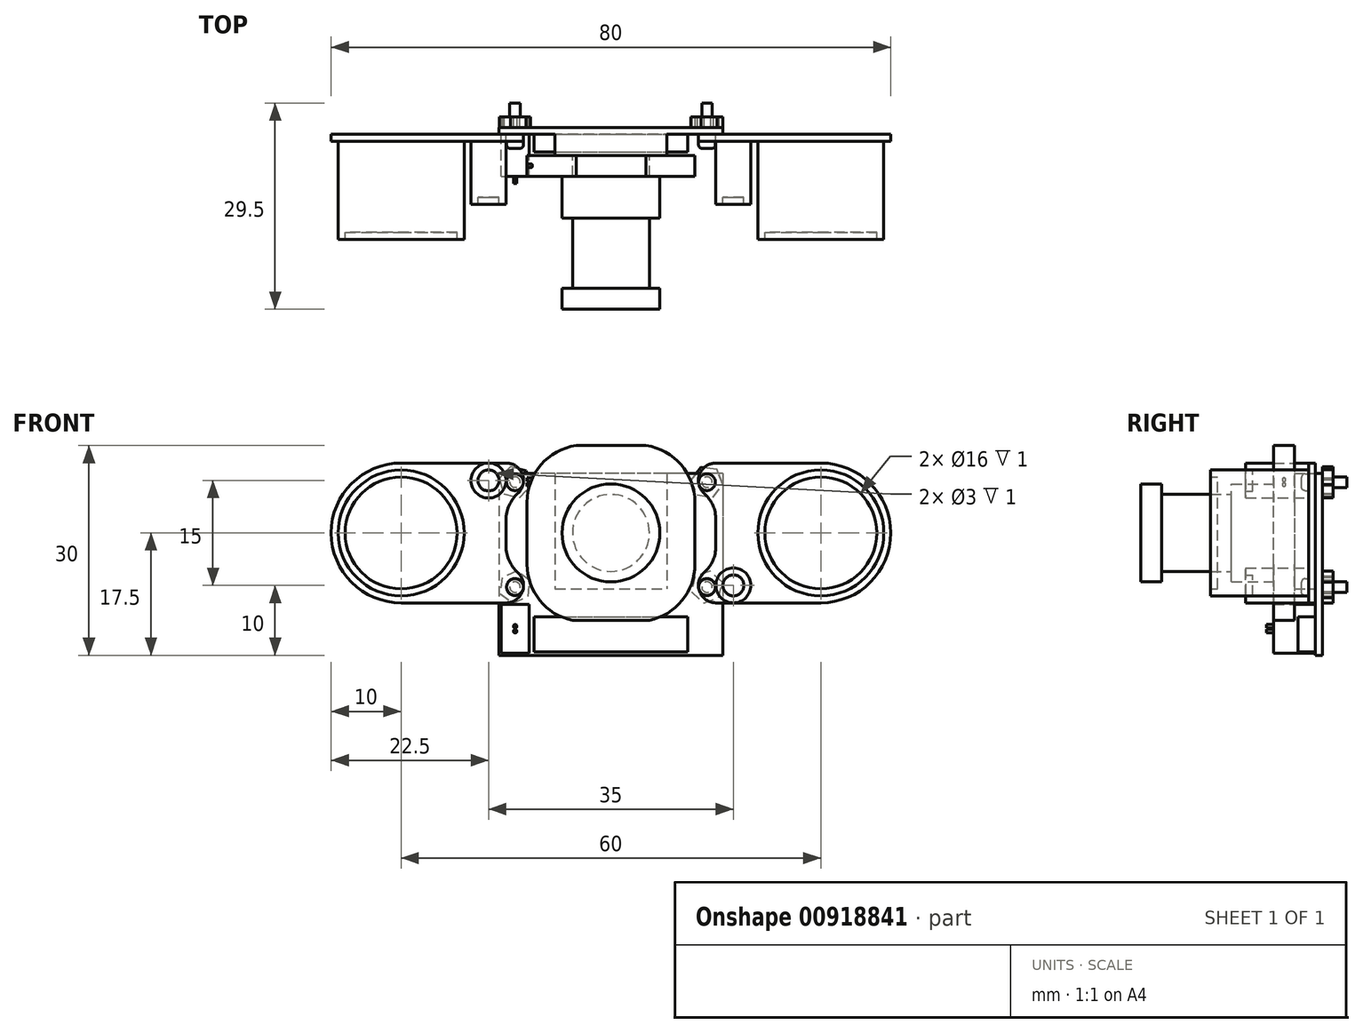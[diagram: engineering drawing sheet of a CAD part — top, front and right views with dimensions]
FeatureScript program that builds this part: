
annotation { "Feature Type Name" : "Feature", "Feature Type Description" : "" }
export const myFeature = defineFeature(function(context is Context, id is Id, definition is map)
    precondition{}
    {
        {
            var Q0;
            Q0=qCreatedBy(makeId("Front.planeOp"),FACE);
            var sketch = newSketch(context, id + "F0", { "sketchPlane" : qUnion([Q0])});
            skLineSegment(sketch, "E0.bottom", {"start": v(16, 13) * mm, "end": v(-16, 13) * mm});
            skLineSegment(sketch, "E0.top", {"start": v(16, -13) * mm, "end": v(-16, -13) * mm});
            skLineSegment(sketch, "E0.left", {"start": v(16, 13) * mm, "end": v(16, -13) * mm});
            skLineSegment(sketch, "E0.right", {"start": v(-16, 13) * mm, "end": v(-16, -13) * mm});
            skPoint(sketch, "E0.middle", {"position": v(0, 0) * mm});
            skSolve(sketch);
        }
        {
            var Q0;
            Q0 = qSketchRegion(id + "F0", true);
            extrude(context, id + "F1", {"entities" : qUnion([Q0]), "depth" : 1 * mm, "offsetDistance" : 25 * mm});
        }
        {
            var Q0;
            Q0=makeQuery(id+"F1.opExtrude","CAP_FACE",FACE,{"disambiguationData":[OSD([sQuery(id+"F0.wireOp",EDGE,"E0.bottom"),sQuery(id+"F0.wireOp",EDGE,"E0.top"),sQuery(id+"F0.wireOp",EDGE,"E0.left"),sQuery(id+"F0.wireOp",EDGE,"E0.right")])],"isStart":false});
            var sketch = newSketch(context, id + "F2", { "sketchPlane" : qUnion([Q0])});
            skLineSegment(sketch, "E1.bottom", {"start": v(-15, 14.5) * mm, "end": v(-30, 14.5) * mm});
            skLineSegment(sketch, "E1.top", {"start": v(-15, -5.5) * mm, "end": v(-30, -5.5) * mm});
            skLineSegment(sketch, "E1.left", {"start": v(-15, 14.5) * mm, "end": v(-15, -5.5) * mm, "construction": true});
            skLineSegment(sketch, "E1.right", {"start": v(-30, 14.5) * mm, "end": v(-30, -5.5) * mm, "construction": true});
            skArc(sketch, "E2", {"start": v(-30, 14.5) * mm, "mid": v(-40, 4.5) * mm, "end": v(-30, -5.5) * mm});
            skArc(sketch, "E3", {"start": v(-13.33, 10.14) * mm, "mid": v(-12.66, 12.9) * mm, "end": v(-15, 14.5) * mm});
            skArc(sketch, "E4", {"start": v(-15, -5.5) * mm, "mid": v(-12.66, -3.9) * mm, "end": v(-13.33, -1.14) * mm});
            skLineSegment(sketch, "E5", {"start": v(-15, 6.4) * mm, "end": v(-15, 2.6) * mm});
            skLineSegment(sketch, "E6", {"start": v(-40, 4.5) * mm, "end": v(-40, 16.6) * mm, "construction": true});
            skPoint(sketch, "E7.visualSharp", {"position": v(-15, 9.5) * mm});
            skArc(sketch, "E7.filletArc", {"start": v(-13.33, 10.14) * mm, "mid": v(-14.56, 8.45) * mm, "end": v(-15, 6.4) * mm});
            skPoint(sketch, "E8.visualSharp", {"position": v(-15, -0.5) * mm});
            skArc(sketch, "E8.filletArc", {"start": v(-15, 2.6) * mm, "mid": v(-14.56, 0.55) * mm, "end": v(-13.33, -1.14) * mm});
            skLineSegment(sketch, "E9", {"start": v(0, 0) * mm, "end": v(0, 30.37) * mm, "construction": true});
            skLineSegment(sketch, "E10.MirrorCS", {"start": v(15, 6.4) * mm, "end": v(15, 2.6) * mm});
            skArc(sketch, "E11.MirrorCS", {"start": v(15, -5.5) * mm, "mid": v(12.66, -3.9) * mm, "end": v(13.33, -1.14) * mm});
            skArc(sketch, "E12.MirrorCS", {"start": v(30, 14.5) * mm, "mid": v(40, 4.5) * mm, "end": v(30, -5.5) * mm});
            skArc(sketch, "E13.MirrorCS", {"start": v(15, 2.6) * mm, "mid": v(14.56, 0.55) * mm, "end": v(13.33, -1.14) * mm});
            skLineSegment(sketch, "E14.MirrorCS", {"start": v(30, 14.5) * mm, "end": v(30, -5.5) * mm, "construction": true});
            skLineSegment(sketch, "E15.MirrorCS", {"start": v(15, 14.5) * mm, "end": v(30, 14.5) * mm});
            skLineSegment(sketch, "E16.MirrorCS", {"start": v(15, 14.5) * mm, "end": v(15, -5.5) * mm, "construction": true});
            skPoint(sketch, "E17.MirrorP", {"position": v(15, 9.5) * mm});
            skArc(sketch, "E18.MirrorCS", {"start": v(13.33, 10.14) * mm, "mid": v(12.66, 12.9) * mm, "end": v(15, 14.5) * mm});
            skArc(sketch, "E19.MirrorCS", {"start": v(13.33, 10.14) * mm, "mid": v(14.56, 8.45) * mm, "end": v(15, 6.4) * mm});
            skLineSegment(sketch, "E20.MirrorCS", {"start": v(40, 4.5) * mm, "end": v(40, 16.6) * mm, "construction": true});
            skPoint(sketch, "E21.MirrorP", {"position": v(15, -0.5) * mm});
            skLineSegment(sketch, "E22.MirrorCS", {"start": v(15, -5.5) * mm, "end": v(30, -5.5) * mm});
            skSolve(sketch);
        }
        {
            var Q0;
            Q0 = qSketchRegion(id + "F2", true);
            extrude(context, id + "F3", {"entities" : qUnion([Q0]), "operationType" : NewBodyOperationType.ADD, "depth" : 1 * mm, "offsetDistance" : 25 * mm});
        }
        {
            var Q0;
            Q0=makeQuery(id+"F3.opExtrude","CAP_FACE",FACE,{"disambiguationData":[OSD([sQuery(id+"F2.wireOp",EDGE,"E1.bottom"),sQuery(id+"F2.wireOp",EDGE,"E1.top"),sQuery(id+"F2.wireOp",EDGE,"E2"),sQuery(id+"F2.wireOp",EDGE,"E3"),sQuery(id+"F2.wireOp",EDGE,"E4"),sQuery(id+"F2.wireOp",EDGE,"E5"),sQuery(id+"F2.wireOp",EDGE,"E7.filletArc"),sQuery(id+"F2.wireOp",EDGE,"E8.filletArc")])],"isStart":false});
            var sketch = newSketch(context, id + "F4", { "sketchPlane" : qUnion([Q0])});
            skCircle(sketch, "E23", {"center": v(-30, 4.5) * mm, "radius": 9 * mm});
            skCircle(sketch, "E24", {"center": v(30, 4.5) * mm, "radius": 9 * mm});
            skCircle(sketch, "E25", {"center": v(-30, 4.5) * mm, "radius": 8 * mm});
            skCircle(sketch, "E26", {"center": v(30, 4.5) * mm, "radius": 8 * mm});
            skSolve(sketch);
        }
        {
            var Q0;
            Q0 = qSketchRegion(id + "F4", true);
            extrude(context, id + "F5", {"entities" : qUnion([Q0]), "operationType" : NewBodyOperationType.ADD, "depth" : 14 * mm, "offsetDistance" : 25 * mm});
        }
        {
            var Q0;
            {var subQ0=sQuery(id+"F2.wireOp",EDGE,"E2");var subQ1=sQuery(id+"F2.wireOp",EDGE,"E1.top");var subQ2=sQuery(id+"F2.wireOp",EDGE,"E3");var subQ3=sQuery(id+"F2.wireOp",EDGE,"E1.bottom");var subQ4=sQuery(id+"F2.wireOp",EDGE,"E4");var subQ5=sQuery(id+"F2.wireOp",EDGE,"E5");var subQ6=sQuery(id+"F2.wireOp",EDGE,"E7.filletArc");var subQ7=sQuery(id+"F2.wireOp",EDGE,"E8.filletArc");Q0=makeQuery(id+"F5.boolean.opBoolean","SPLIT",FACE,{"disambiguationData":[TD([makeQuery(id+"F3.opExtrude","SWEPT_FACE",FACE,{"disambiguationData":[OSD([subQ3])]})])],"derivedFrom":makeQuery(id+"F3.opExtrude","CAP_FACE",FACE,{"disambiguationData":[OSD([subQ3,subQ1,subQ0,subQ2,subQ4,subQ5,subQ6,subQ7])],"isStart":false})});}
            var sketch = newSketch(context, id + "F6", { "sketchPlane" : qUnion([Q0])});
            skCircle(sketch, "E27", {"center": v(-17.5, 12) * mm, "radius": 2.5 * mm});
            skCircle(sketch, "E28", {"center": v(17.5, -3) * mm, "radius": 2.5 * mm});
            skCircle(sketch, "E29", {"center": v(-17.5, 12) * mm, "radius": 1.5 * mm});
            skCircle(sketch, "E30", {"center": v(17.5, -3) * mm, "radius": 1.5 * mm});
            skSolve(sketch);
        }
        {
            var Q0;
            Q0 = qSketchRegion(id + "F6", true);
            extrude(context, id + "F7", {"entities" : qUnion([Q0]), "operationType" : NewBodyOperationType.ADD, "depth" : 9 * mm, "offsetDistance" : 25 * mm});
        }
        {
            var Q0;
            Q0=makeQuery(id+"F1.opExtrude","CAP_FACE",FACE,{"disambiguationData":[OSD([sQuery(id+"F0.wireOp",EDGE,"E0.bottom"),sQuery(id+"F0.wireOp",EDGE,"E0.top"),sQuery(id+"F0.wireOp",EDGE,"E0.left"),sQuery(id+"F0.wireOp",EDGE,"E0.right")])],"isStart":false});
            var sketch = newSketch(context, id + "F8", { "sketchPlane" : qUnion([Q0])});
            skLineSegment(sketch, "E31.bottom", {"start": v(-11, -7.5) * mm, "end": v(11, -7.5) * mm});
            skLineSegment(sketch, "E31.top", {"start": v(-11, -12.5) * mm, "end": v(11, -12.5) * mm});
            skLineSegment(sketch, "E31.left", {"start": v(-11, -7.5) * mm, "end": v(-11, -12.5) * mm});
            skLineSegment(sketch, "E31.right", {"start": v(11, -7.5) * mm, "end": v(11, -12.5) * mm});
            skSolve(sketch);
        }
        {
            var Q0;
            Q0 = qSketchRegion(id + "F8", true);
            extrude(context, id + "F9", {"entities" : qUnion([Q0]), "operationType" : NewBodyOperationType.ADD, "depth" : 2.5 * mm, "offsetDistance" : 25 * mm});
        }
        {
            var Q0;
            Q0=makeQuery(id+"F1.opExtrude","CAP_FACE",FACE,{"disambiguationData":[OSD([sQuery(id+"F0.wireOp",EDGE,"E0.bottom"),sQuery(id+"F0.wireOp",EDGE,"E0.top"),sQuery(id+"F0.wireOp",EDGE,"E0.left"),sQuery(id+"F0.wireOp",EDGE,"E0.right")])],"isStart":false});
            var sketch = newSketch(context, id + "F10", { "sketchPlane" : qUnion([Q0])});
            skLineSegment(sketch, "E32.bottom", {"start": v(-8, 13) * mm, "end": v(8, 13) * mm});
            skLineSegment(sketch, "E32.top", {"start": v(-8, -3.5) * mm, "end": v(8, -3.5) * mm});
            skLineSegment(sketch, "E32.left", {"start": v(-8, 13) * mm, "end": v(-8, -3.5) * mm});
            skLineSegment(sketch, "E32.right", {"start": v(8, 13) * mm, "end": v(8, -3.5) * mm});
            skLineSegment(sketch, "E33", {"start": v(0, 13) * mm, "end": v(0, -3.5) * mm, "construction": true});
            skSolve(sketch);
        }
        {
            var Q0;
            Q0 = qSketchRegion(id + "F10", true);
            extrude(context, id + "F11", {"entities" : qUnion([Q0]), "operationType" : NewBodyOperationType.ADD, "depth" : 3 * mm, "offsetDistance" : 25 * mm});
        }
        {
            var Q0;
            Q0=makeQuery(id+"F11.opExtrude","CAP_FACE",FACE,{"disambiguationData":[OSD([sQuery(id+"F10.wireOp",EDGE,"E32.bottom"),sQuery(id+"F10.wireOp",EDGE,"E32.top"),sQuery(id+"F10.wireOp",EDGE,"E32.left"),sQuery(id+"F10.wireOp",EDGE,"E32.right")])],"isStart":false});
            var sketch = newSketch(context, id + "F12", { "sketchPlane" : qUnion([Q0])});
            skLineSegment(sketch, "E34.bottom", {"start": v(-12, 17) * mm, "end": v(12, 17) * mm, "construction": true});
            skLineSegment(sketch, "E34.top", {"start": v(-12, -8) * mm, "end": v(12, -8) * mm, "construction": true});
            skLineSegment(sketch, "E34.left", {"start": v(-12, 17) * mm, "end": v(-12, -8) * mm, "construction": true});
            skLineSegment(sketch, "E34.right", {"start": v(12, 17) * mm, "end": v(12, -8) * mm, "construction": true});
            skArc(sketch, "E35", {"start": v(-5, 17) * mm, "mid": v(-10, 14.26) * mm, "end": v(-12, 8.91) * mm});
            skArc(sketch, "E36", {"start": v(12, 8.91) * mm, "mid": v(10, 14.26) * mm, "end": v(5, 17) * mm});
            skArc(sketch, "E37", {"start": v(-12, 0) * mm, "mid": v(-10.17, -5.15) * mm, "end": v(-5.5, -8) * mm});
            skArc(sketch, "E38", {"start": v(5.5, -8) * mm, "mid": v(10.17, -5.15) * mm, "end": v(12, 0) * mm});
            skLineSegment(sketch, "E39", {"start": v(0, 17) * mm, "end": v(0, -8) * mm, "construction": true});
            skLineSegment(sketch, "E40", {"start": v(-12, 8.91) * mm, "end": v(-12, 0) * mm});
            skLineSegment(sketch, "E41", {"start": v(-5.5, -8) * mm, "end": v(5.5, -8) * mm});
            skLineSegment(sketch, "E42", {"start": v(12, 0) * mm, "end": v(12, 8.91) * mm});
            skLineSegment(sketch, "E43", {"start": v(5, 17) * mm, "end": v(-5, 17) * mm});
            skSolve(sketch);
        }
        {
            var Q0;
            Q0 = qSketchRegion(id + "F12", true);
            extrude(context, id + "F13", {"entities" : qUnion([Q0]), "operationType" : NewBodyOperationType.ADD, "depth" : 3 * mm, "offsetDistance" : 25 * mm});
        }
        {
            var Q0;
            Q0=makeQuery(id+"F13.opExtrude","CAP_FACE",FACE,{"disambiguationData":[OSD([sQuery(id+"F12.wireOp",EDGE,"E35"),sQuery(id+"F12.wireOp",EDGE,"E36"),sQuery(id+"F12.wireOp",EDGE,"E37"),sQuery(id+"F12.wireOp",EDGE,"E38"),sQuery(id+"F12.wireOp",EDGE,"E40"),sQuery(id+"F12.wireOp",EDGE,"E41"),sQuery(id+"F12.wireOp",EDGE,"E42"),sQuery(id+"F12.wireOp",EDGE,"E43")])],"isStart":false});
            var sketch = newSketch(context, id + "F14", { "sketchPlane" : qUnion([Q0])});
            skCircle(sketch, "E44", {"center": v(0, 4.5) * mm, "radius": 7 * mm});
            skLineSegment(sketch, "E45", {"start": v(0, -8) * mm, "end": v(0, 17) * mm, "construction": true});
            skSolve(sketch);
        }
        {
            var Q0;
            Q0 = qSketchRegion(id + "F14", true);
            extrude(context, id + "F15", {"entities" : qUnion([Q0]), "operationType" : NewBodyOperationType.ADD, "depth" : 6 * mm, "offsetDistance" : 25 * mm});
        }
        {
            var Q0;
            Q0=makeQuery(id+"F15.opExtrude","CAP_FACE",FACE,{"disambiguationData":[OSD([sQuery(id+"F14.wireOp",EDGE,"E44")])],"isStart":false});
            var sketch = newSketch(context, id + "F16", { "sketchPlane" : qUnion([Q0])});
            skCircle(sketch, "E46", {"center": v(0, 4.5) * mm, "radius": 5.5 * mm});
            skSolve(sketch);
        }
        {
            var Q0;
            Q0 = qSketchRegion(id + "F16", true);
            extrude(context, id + "F17", {"entities" : qUnion([Q0]), "operationType" : NewBodyOperationType.ADD, "depth" : 10 * mm, "offsetDistance" : 25 * mm});
        }
        {
            var Q0;
            Q0=makeQuery(id+"F17.opExtrude","CAP_FACE",FACE,{"disambiguationData":[OSD([sQuery(id+"F16.wireOp",EDGE,"E46")])],"isStart":false});
            var sketch = newSketch(context, id + "F18", { "sketchPlane" : qUnion([Q0])});
            skCircle(sketch, "E47", {"center": v(0, 4.5) * mm, "radius": 7 * mm});
            skSolve(sketch);
        }
        {
            var Q0;
            Q0 = qSketchRegion(id + "F18", true);
            extrude(context, id + "F19", {"entities" : qUnion([Q0]), "operationType" : NewBodyOperationType.ADD, "depth" : 3 * mm, "offsetDistance" : 25 * mm});
        }
        {
            var Q0;
            Q0=makeQuery(id+"F5.boolean.opBoolean","SPLIT",FACE,{"disambiguationData":[TD([makeQuery(id+"F5.opExtrude","SWEPT_FACE",FACE,{"disambiguationData":[OSD([sQuery(id+"F4.wireOp",EDGE,"E25")])]})])],"derivedFrom":makeQuery(id+"F3.opExtrude","CAP_FACE",FACE,{"disambiguationData":[OSD([sQuery(id+"F2.wireOp",EDGE,"E1.bottom"),sQuery(id+"F2.wireOp",EDGE,"E1.top"),sQuery(id+"F2.wireOp",EDGE,"E2"),sQuery(id+"F2.wireOp",EDGE,"E3"),sQuery(id+"F2.wireOp",EDGE,"E4"),sQuery(id+"F2.wireOp",EDGE,"E5"),sQuery(id+"F2.wireOp",EDGE,"E7.filletArc"),sQuery(id+"F2.wireOp",EDGE,"E8.filletArc")])],"isStart":false})});
            var Q1;
            Q1=makeQuery(id+"F5.boolean.opBoolean","SPLIT",FACE,{"disambiguationData":[TD([makeQuery(id+"F5.opExtrude","SWEPT_FACE",FACE,{"disambiguationData":[OSD([sQuery(id+"F4.wireOp",EDGE,"E26")])]})])],"derivedFrom":makeQuery(id+"F3.opExtrude","CAP_FACE",FACE,{"disambiguationData":[OSD([sQuery(id+"F2.wireOp",EDGE,"E10.MirrorCS"),sQuery(id+"F2.wireOp",EDGE,"E11.MirrorCS"),sQuery(id+"F2.wireOp",EDGE,"E12.MirrorCS"),sQuery(id+"F2.wireOp",EDGE,"E13.MirrorCS"),sQuery(id+"F2.wireOp",EDGE,"E15.MirrorCS"),sQuery(id+"F2.wireOp",EDGE,"E18.MirrorCS"),sQuery(id+"F2.wireOp",EDGE,"E19.MirrorCS"),sQuery(id+"F2.wireOp",EDGE,"E22.MirrorCS")])],"isStart":false})});
            extrude(context, id + "F20", {"entities" : qUnion([Q0, Q1]), "operationType" : NewBodyOperationType.ADD, "depth" : 13 * mm, "offsetDistance" : 25 * mm});
        }
        {
            var Q0;
            {var subQ0=sQuery(id+"F2.wireOp",EDGE,"E12.MirrorCS");var subQ1=sQuery(id+"F2.wireOp",EDGE,"E11.MirrorCS");var subQ2=sQuery(id+"F2.wireOp",EDGE,"E13.MirrorCS");var subQ3=sQuery(id+"F2.wireOp",EDGE,"E10.MirrorCS");var subQ4=sQuery(id+"F2.wireOp",EDGE,"E15.MirrorCS");var subQ5=sQuery(id+"F2.wireOp",EDGE,"E18.MirrorCS");var subQ6=sQuery(id+"F2.wireOp",EDGE,"E19.MirrorCS");var subQ7=sQuery(id+"F2.wireOp",EDGE,"E22.MirrorCS");Q0=makeQuery(id+"F7.boolean.opBoolean","SPLIT",FACE,{"disambiguationData":[TD([makeQuery(id+"F7.opExtrude","SWEPT_FACE",FACE,{"disambiguationData":[OSD([sQuery(id+"F6.wireOp",EDGE,"E30")])]})])],"derivedFrom":makeQuery(id+"F5.boolean.opBoolean","SPLIT",FACE,{"disambiguationData":[TD([makeQuery(id+"F3.opExtrude","SWEPT_FACE",FACE,{"disambiguationData":[OSD([subQ3])]})])],"derivedFrom":makeQuery(id+"F3.opExtrude","CAP_FACE",FACE,{"disambiguationData":[OSD([subQ3,subQ1,subQ0,subQ2,subQ4,subQ5,subQ6,subQ7])],"isStart":false})})});}
            var Q1;
            {var subQ0=sQuery(id+"F2.wireOp",EDGE,"E2");var subQ1=sQuery(id+"F2.wireOp",EDGE,"E1.top");var subQ2=sQuery(id+"F2.wireOp",EDGE,"E3");var subQ3=sQuery(id+"F2.wireOp",EDGE,"E1.bottom");var subQ4=sQuery(id+"F2.wireOp",EDGE,"E4");var subQ5=sQuery(id+"F2.wireOp",EDGE,"E5");var subQ6=sQuery(id+"F2.wireOp",EDGE,"E7.filletArc");var subQ7=sQuery(id+"F2.wireOp",EDGE,"E8.filletArc");Q1=makeQuery(id+"F7.boolean.opBoolean","SPLIT",FACE,{"disambiguationData":[TD([makeQuery(id+"F7.opExtrude","SWEPT_FACE",FACE,{"disambiguationData":[OSD([sQuery(id+"F6.wireOp",EDGE,"E29")])]})])],"derivedFrom":makeQuery(id+"F5.boolean.opBoolean","SPLIT",FACE,{"disambiguationData":[TD([makeQuery(id+"F3.opExtrude","SWEPT_FACE",FACE,{"disambiguationData":[OSD([subQ3])]})])],"derivedFrom":makeQuery(id+"F3.opExtrude","CAP_FACE",FACE,{"disambiguationData":[OSD([subQ3,subQ1,subQ0,subQ2,subQ4,subQ5,subQ6,subQ7])],"isStart":false})})});}
            extrude(context, id + "F21", {"entities" : qUnion([Q0, Q1]), "operationType" : NewBodyOperationType.ADD, "depth" : 8 * mm, "offsetDistance" : 25 * mm});
        }
        {
            var Q0;
            {var subQ0=sQuery(id+"F2.wireOp",EDGE,"E2");var subQ2=sQuery(id+"F2.wireOp",EDGE,"E1.top");var subQ4=sQuery(id+"F2.wireOp",EDGE,"E3");var subQ7=sQuery(id+"F2.wireOp",EDGE,"E1.bottom");var subQ8=makeQuery(id+"F3.opExtrude","SWEPT_FACE",FACE,{"disambiguationData":[OSD([subQ7])]});var subQ9=sQuery(id+"F2.wireOp",EDGE,"E4");var subQ11=sQuery(id+"F2.wireOp",EDGE,"E5");var subQ13=sQuery(id+"F2.wireOp",EDGE,"E7.filletArc");var subQ15=sQuery(id+"F2.wireOp",EDGE,"E8.filletArc");Q0=makeQuery(id+"F7.boolean.opBoolean","SPLIT",FACE,{"disambiguationData":[TD([subQ8])],"derivedFrom":makeQuery(id+"F5.boolean.opBoolean","SPLIT",FACE,{"disambiguationData":[TD([subQ8])],"derivedFrom":makeQuery(id+"F3.opExtrude","CAP_FACE",FACE,{"disambiguationData":[OSD([subQ7,subQ2,subQ0,subQ4,subQ9,subQ11,subQ13,subQ15])],"isStart":false})})});}
            var sketch = newSketch(context, id + "F22", { "sketchPlane" : qUnion([Q0])});
            skCircle(sketch, "E48", {"center": v(-13.72, 11.76) * mm, "radius": 1.2 * mm});
            skCircle(sketch, "E49", {"center": v(-13.72, -3.24) * mm, "radius": 1.2 * mm});
            skPoint(sketch, "E49.centerSnap0", {"position": v(-14.56, 0.55) * mm});
            skCircle(sketch, "E50", {"center": v(13.72, 11.76) * mm, "radius": 1.2 * mm});
            skCircle(sketch, "E51", {"center": v(13.72, -3.24) * mm, "radius": 1.2 * mm});
            skLineSegment(sketch, "E52", {"start": v(-13.72, 11.76) * mm, "end": v(-13.72, -3.24) * mm, "construction": true});
            skLineSegment(sketch, "E53", {"start": v(13.72, 11.76) * mm, "end": v(13.72, -3.24) * mm, "construction": true});
            skLineSegment(sketch, "E54", {"start": v(-13.72, 11.76) * mm, "end": v(13.72, 11.76) * mm, "construction": true});
            skSolve(sketch);
        }
        {
            var Q0;
            Q0 = qSketchRegion(id + "F22", true);
            extrude(context, id + "F23", {"entities" : qUnion([Q0]), "operationType" : NewBodyOperationType.ADD, "depth" : 1 * mm, "offsetDistance" : 25 * mm});
        }
        {
            var Q0;
            Q0=makeQuery(id+"F23.opExtrude","CAP_FACE",FACE,{"disambiguationData":[OSD([sQuery(id+"F22.wireOp",EDGE,"E48")])],"isStart":false});
            var Q1;
            Q1=makeQuery(id+"F23.opExtrude","CAP_FACE",FACE,{"disambiguationData":[OSD([sQuery(id+"F22.wireOp",EDGE,"E49")])],"isStart":false});
            var Q2;
            Q2=makeQuery(id+"F23.opExtrude","CAP_FACE",FACE,{"disambiguationData":[OSD([sQuery(id+"F22.wireOp",EDGE,"E50")])],"isStart":false});
            var Q3;
            Q3=makeQuery(id+"F23.opExtrude","CAP_FACE",FACE,{"disambiguationData":[OSD([sQuery(id+"F22.wireOp",EDGE,"E51")])],"isStart":false});
            fillet(context, id + "F24", {"entities" : qUnion([Q0, Q1, Q2, Q3]), "radius" : 0.5 * mm, "tangentPropagation" : true, "allowEdgeOverflow" : false});
        }
        {
            var Q0;
            Q0=makeQuery(id+"F1.opExtrude","CAP_FACE",FACE,{"disambiguationData":[OSD([sQuery(id+"F0.wireOp",EDGE,"E0.bottom"),sQuery(id+"F0.wireOp",EDGE,"E0.top"),sQuery(id+"F0.wireOp",EDGE,"E0.left"),sQuery(id+"F0.wireOp",EDGE,"E0.right")])],"isStart":true});
            var sketch = newSketch(context, id + "F25", { "sketchPlane" : qUnion([Q0])});
            skCircle(sketch, "E55.cCircle", {"center": v(-13.72, 11.76) * mm, "radius": 2 * mm, "construction": true});
            skLineSegment(sketch, "E55.0", {"start": v(-16, 11.43) * mm, "end": v(-15.15, 13.57) * mm});
            skLineSegment(sketch, "E55.1", {"start": v(-15.15, 13.57) * mm, "end": v(-12.86, 13.9) * mm});
            skLineSegment(sketch, "E55.2", {"start": v(-12.86, 13.9) * mm, "end": v(-11.44, 12.09) * mm});
            skLineSegment(sketch, "E55.3", {"start": v(-11.44, 12.09) * mm, "end": v(-12.3, 9.94) * mm});
            skLineSegment(sketch, "E55.4", {"start": v(-12.3, 9.94) * mm, "end": v(-14.58, 9.61) * mm});
            skLineSegment(sketch, "E55.5", {"start": v(-14.58, 9.61) * mm, "end": v(-16, 11.43) * mm});
            skPoint(sketch, "E55.0.midPoint", {"position": v(-15.58, 12.5) * mm});
            skCircle(sketch, "E56.cCircle", {"center": v(13.72, 11.76) * mm, "radius": 2 * mm, "construction": true});
            skLineSegment(sketch, "E56.0", {"start": v(15.96, 12.32) * mm, "end": v(15.33, 10.1) * mm});
            skLineSegment(sketch, "E56.1", {"start": v(15.33, 10.1) * mm, "end": v(13.1, 9.54) * mm});
            skLineSegment(sketch, "E56.2", {"start": v(13.1, 9.54) * mm, "end": v(11.48, 11.2) * mm});
            skLineSegment(sketch, "E56.3", {"start": v(11.48, 11.2) * mm, "end": v(12.12, 13.42) * mm});
            skLineSegment(sketch, "E56.4", {"start": v(12.12, 13.42) * mm, "end": v(14.36, 13.98) * mm});
            skLineSegment(sketch, "E56.5", {"start": v(14.36, 13.98) * mm, "end": v(15.96, 12.32) * mm});
            skPoint(sketch, "E56.0.midPoint", {"position": v(15.65, 11.21) * mm});
            skCircle(sketch, "E57.cCircle", {"center": v(-13.72, -3.24) * mm, "radius": 2 * mm, "construction": true});
            skLineSegment(sketch, "E57.0", {"start": v(-11.53, -3.97) * mm, "end": v(-13.25, -5.5) * mm});
            skLineSegment(sketch, "E57.1", {"start": v(-13.25, -5.5) * mm, "end": v(-15.45, -4.78) * mm});
            skLineSegment(sketch, "E57.2", {"start": v(-15.45, -4.78) * mm, "end": v(-15.92, -2.52) * mm});
            skLineSegment(sketch, "E57.3", {"start": v(-15.92, -2.52) * mm, "end": v(-14.2, -0.98) * mm});
            skLineSegment(sketch, "E57.4", {"start": v(-14.2, -0.98) * mm, "end": v(-12, -1.7) * mm});
            skLineSegment(sketch, "E57.5", {"start": v(-12, -1.7) * mm, "end": v(-11.53, -3.97) * mm});
            skPoint(sketch, "E57.0.midPoint", {"position": v(-12.4, -4.73) * mm});
            skCircle(sketch, "E58.cCircle", {"center": v(13.72, -3.24) * mm, "radius": 2 * mm, "construction": true});
            skLineSegment(sketch, "E58.0", {"start": v(15.83, -4.2) * mm, "end": v(13.95, -5.54) * mm});
            skLineSegment(sketch, "E58.1", {"start": v(13.95, -5.54) * mm, "end": v(11.85, -4.59) * mm});
            skLineSegment(sketch, "E58.2", {"start": v(11.85, -4.59) * mm, "end": v(11.62, -2.29) * mm});
            skLineSegment(sketch, "E58.3", {"start": v(11.62, -2.29) * mm, "end": v(13.5, -0.94) * mm});
            skLineSegment(sketch, "E58.4", {"start": v(13.5, -0.94) * mm, "end": v(15.6, -1.9) * mm});
            skLineSegment(sketch, "E58.5", {"start": v(15.6, -1.9) * mm, "end": v(15.83, -4.2) * mm});
            skPoint(sketch, "E58.0.midPoint", {"position": v(14.89, -4.87) * mm});
            skSolve(sketch);
        }
        {
            var Q0;
            Q0 = qSketchRegion(id + "F25", true);
            extrude(context, id + "F26", {"entities" : qUnion([Q0]), "operationType" : NewBodyOperationType.ADD, "depth" : 1.5 * mm, "offsetDistance" : 25 * mm});
        }
        {
            var Q0;
            Q0=makeQuery(id+"F26.opExtrude","CAP_FACE",FACE,{"disambiguationData":[OSD([sQuery(id+"F25.wireOp",EDGE,"E55.0"),sQuery(id+"F25.wireOp",EDGE,"E55.1"),sQuery(id+"F25.wireOp",EDGE,"E55.2"),sQuery(id+"F25.wireOp",EDGE,"E55.3"),sQuery(id+"F25.wireOp",EDGE,"E55.4"),sQuery(id+"F25.wireOp",EDGE,"E55.5")])],"isStart":false});
            var sketch = newSketch(context, id + "F27", { "sketchPlane" : qUnion([Q0])});
            skCircle(sketch, "E59", {"center": v(-13.72, 11.76) * mm, "radius": 0.75 * mm});
            skCircle(sketch, "E60", {"center": v(-13.72, -3.24) * mm, "radius": 0.75 * mm});
            skCircle(sketch, "E61", {"center": v(13.72, -3.24) * mm, "radius": 0.75 * mm});
            skCircle(sketch, "E62", {"center": v(13.72, 11.76) * mm, "radius": 0.75 * mm});
            skSolve(sketch);
        }
        {
            var Q0;
            Q0 = qSketchRegion(id + "F27", true);
            extrude(context, id + "F28", {"entities" : qUnion([Q0]), "operationType" : NewBodyOperationType.ADD, "depth" : 2 * mm, "offsetDistance" : 25 * mm});
        }
        {
            var Q0;
            Q0=makeQuery(id+"F1.opExtrude","CAP_FACE",FACE,{"disambiguationData":[OSD([sQuery(id+"F0.wireOp",EDGE,"E0.bottom"),sQuery(id+"F0.wireOp",EDGE,"E0.top"),sQuery(id+"F0.wireOp",EDGE,"E0.left"),sQuery(id+"F0.wireOp",EDGE,"E0.right")])],"isStart":false});
            var sketch = newSketch(context, id + "F29", { "sketchPlane" : qUnion([Q0])});
            skLineSegment(sketch, "E63.bottom", {"start": v(-15.7, -5.7) * mm, "end": v(-11.7, -5.7) * mm});
            skLineSegment(sketch, "E63.top", {"start": v(-15.7, -12.7) * mm, "end": v(-11.7, -12.7) * mm});
            skLineSegment(sketch, "E63.left", {"start": v(-15.7, -5.7) * mm, "end": v(-15.7, -12.7) * mm});
            skLineSegment(sketch, "E63.right", {"start": v(-11.7, -5.7) * mm, "end": v(-11.7, -12.7) * mm});
            skSolve(sketch);
        }
        {
            var Q0;
            Q0 = qSketchRegion(id + "F29", true);
            extrude(context, id + "F30", {"entities" : qUnion([Q0]), "operationType" : NewBodyOperationType.ADD, "depth" : 6 * mm, "offsetDistance" : 25 * mm});
        }
        {
            var Q0;
            Q0=makeQuery(id+"F13.opExtrude","SWEPT_FACE",FACE,{"disambiguationData":[OSD([sQuery(id+"F12.wireOp",EDGE,"E40")])]});
            var sketch = newSketch(context, id + "F31", { "sketchPlane" : qUnion([Q0])});
            skCircle(sketch, "E64", {"center": v(5.5, 12.11) * mm, "radius": 0.25 * mm});
            skPoint(sketch, "E64.centerSnap0", {"position": v(5.5, 8.91) * mm});
            skCircle(sketch, "E65", {"center": v(5.5, 11.41) * mm, "radius": 0.25 * mm});
            skLineSegment(sketch, "E66", {"start": v(5.5, 12.11) * mm, "end": v(5.5, 11.41) * mm, "construction": true});
            skLineSegment(sketch, "E67", {"start": v(5.5, 8.91) * mm, "end": v(5.5, 11.41) * mm, "construction": true});
            skSolve(sketch);
        }
        {
            var Q0;
            Q0 = qSketchRegion(id + "F31", true);
            extrude(context, id + "F32", {"entities" : qUnion([Q0]), "operationType" : NewBodyOperationType.ADD, "oppositeDirection" : true, "depth" : 2 * mm, "offsetDistance" : 25 * mm});
        }
        {
            var Q0;
            Q0=makeQuery(id+"F30.opExtrude","CAP_FACE",FACE,{"disambiguationData":[OSD([sQuery(id+"F29.wireOp",EDGE,"E63.bottom"),sQuery(id+"F29.wireOp",EDGE,"E63.top"),sQuery(id+"F29.wireOp",EDGE,"E63.left"),sQuery(id+"F29.wireOp",EDGE,"E63.right")])],"isStart":false});
            var sketch = newSketch(context, id + "F33", { "sketchPlane" : qUnion([Q0])});
            skCircle(sketch, "E68", {"center": v(-13.7, -8.85) * mm, "radius": 0.25 * mm});
            skCircle(sketch, "E69", {"center": v(-13.7, -9.55) * mm, "radius": 0.25 * mm});
            skLineSegment(sketch, "E70", {"start": v(-13.7, -8.85) * mm, "end": v(-13.7, -9.55) * mm, "construction": true});
            skLineSegment(sketch, "E71", {"start": v(-13.7, -9.2) * mm, "end": v(-11.7, -9.2) * mm, "construction": true});
            skSolve(sketch);
        }
        {
            var Q0;
            Q0 = qSketchRegion(id + "F33", true);
            extrude(context, id + "F34", {"entities" : qUnion([Q0]), "operationType" : NewBodyOperationType.ADD, "depth" : 1 * mm, "offsetDistance" : 25 * mm});
        }
        {
            var Q0;
            Q0=makeQuery(id+"F34.opExtrude","CAP_FACE",FACE,{"disambiguationData":[OSD([sQuery(id+"F33.wireOp",EDGE,"E68")])],"isStart":false});
            var sketch = newSketch(context, id + "F35", { "sketchPlane" : qUnion([Q0])});
            skPoint(sketch, "E72", {"position": v(-13.7, -8.85) * mm});
            skSolve(sketch);
        }
    });
